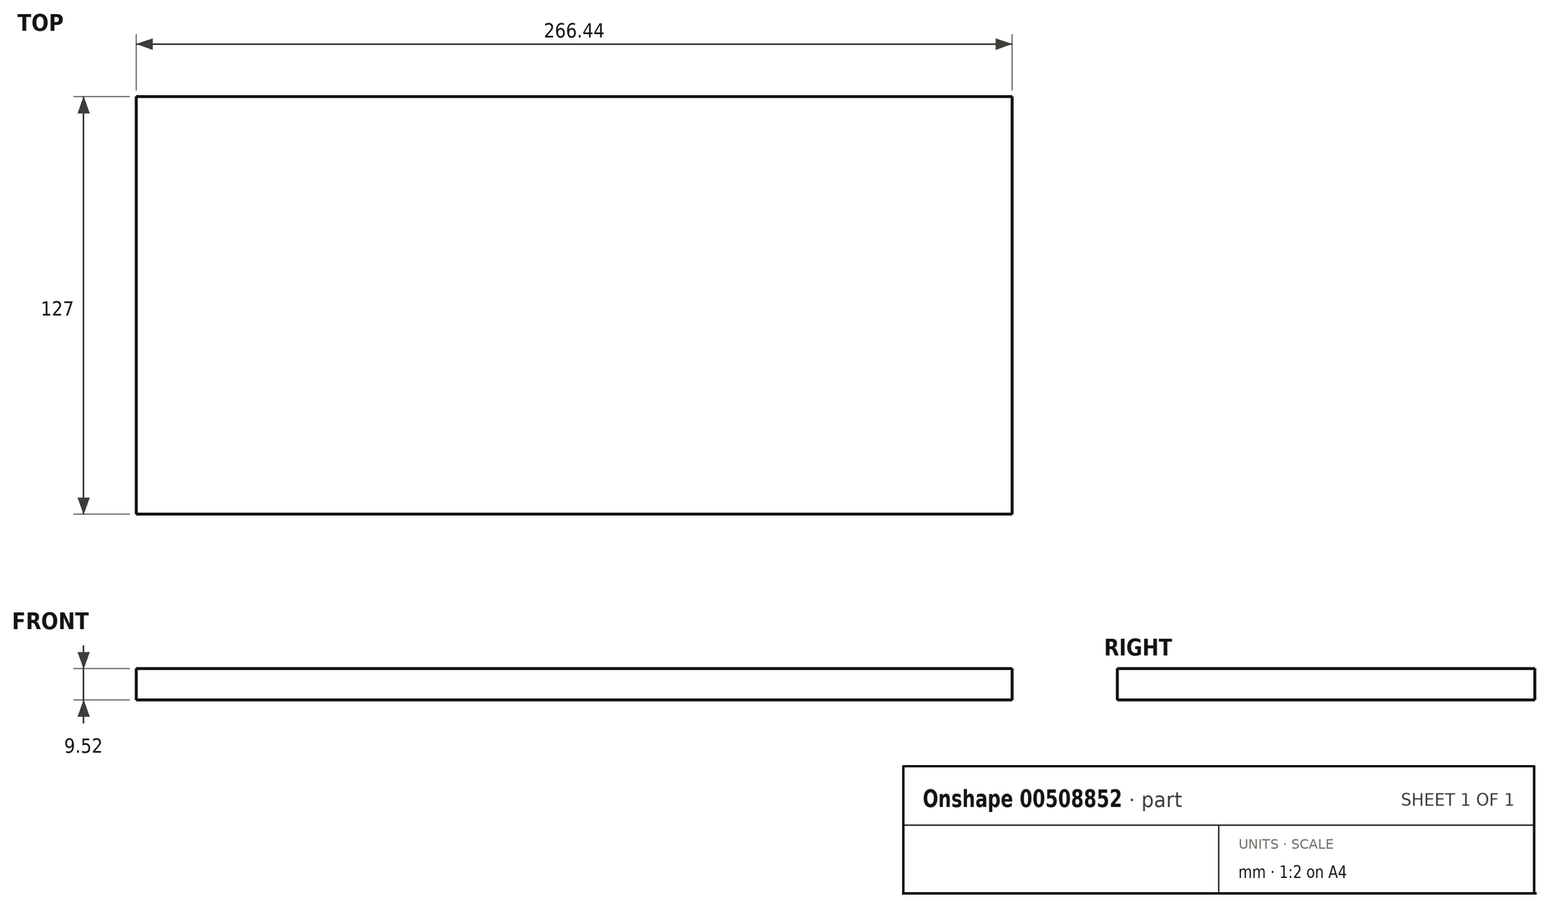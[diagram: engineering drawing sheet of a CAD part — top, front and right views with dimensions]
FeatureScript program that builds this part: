
annotation { "Feature Type Name" : "Feature", "Feature Type Description" : "" }
export const myFeature = defineFeature(function(context is Context, id is Id, definition is map)
    precondition{}
    {
        {
            var Q0;
            Q0=qCreatedBy(makeId("Top.planeOp"),FACE);
            var sketch = newSketch(context, id + "F0", { "sketchPlane" : qUnion([Q0])});
            skLineSegment(sketch, "E0.bottom", {"start": v(133.22, 63.5) * mm, "end": v(-133.22, 63.5) * mm});
            skLineSegment(sketch, "E0.top", {"start": v(133.22, -63.5) * mm, "end": v(-133.22, -63.5) * mm});
            skLineSegment(sketch, "E0.left", {"start": v(133.22, 63.5) * mm, "end": v(133.22, -63.5) * mm});
            skLineSegment(sketch, "E0.right", {"start": v(-133.22, 63.5) * mm, "end": v(-133.22, -63.5) * mm});
            skPoint(sketch, "E0.middle", {"position": v(0, 0) * mm});
            skSolve(sketch);
        }
        {
            var Q0;
            Q0=makeQuery(id+"F0.imprint","IMPRINT",FACE,{"disambiguationData":[TD([[makeQuery(id+"F0.imprint","IMPRINT",EDGE,{"derivedFrom":sQuery(id+"F0.wireOp",EDGE,"E0.bottom")}),1.0]])]});
            extrude(context, id + "F1", {"entities" : qUnion([Q0]), "endBound" : BoundingType.SYMMETRIC, "depth" : 9.52 * mm});
        }
    });
